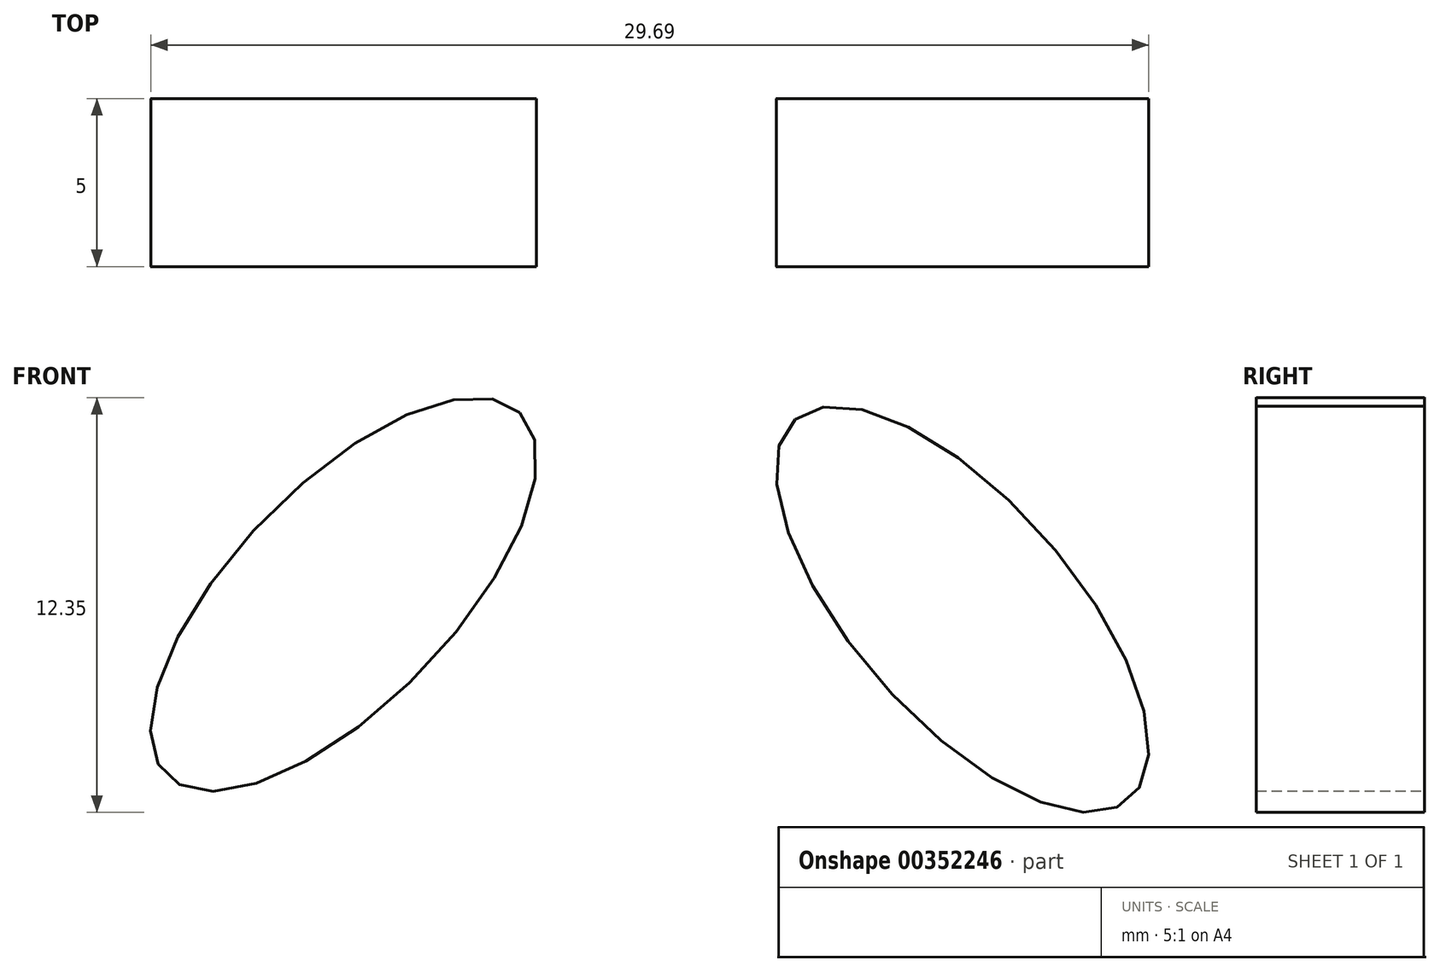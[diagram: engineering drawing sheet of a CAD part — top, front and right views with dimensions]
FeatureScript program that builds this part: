
annotation { "Feature Type Name" : "Feature", "Feature Type Description" : "" }
export const myFeature = defineFeature(function(context is Context, id is Id, definition is map)
    precondition{}
    {
        {
            var Q0;
            Q0=qCreatedBy(makeId("Front.planeOp"),FACE);
            var sketch = newSketch(context, id + "F0", { "sketchPlane" : qUnion([Q0])});
            skArc(sketch, "E0", {"start": v(-19.63, 15.48) * mm, "mid": v(-5.3, -24.43) * mm, "end": v(24.28, 5.97) * mm});
            skArc(sketch, "E1", {"start": v(-19.48, 0) * mm, "mid": v(1, -19.93) * mm, "end": v(21.47, 0) * mm});
            skFitSpline(sketch, "E2", {"points": [v(-19.48, 0) * mm, v(-9.63, -10.16) * mm, v(4.6, -12.46) * mm, v(15.7, -7.75) * mm, v(21.47, 0) * mm], "startDerivative": vector(32.51, -44.35) * mm, "endDerivative": vector(22.17, 38.02) * mm});
            skCircle(sketch, "E3", {"center": v(0, 0) * mm, "radius": 3.48 * mm});
            skFitSpline(sketch, "E4", {"points": [v(-19.63, 15.48) * mm, v(-28.7, 37.07) * mm, v(-14.36, 20.47) * mm, v(-13.3, 37.8) * mm, v(-6.26, 24.2) * mm, v(4.92, 39.9) * mm, v(10.04, 22.9) * mm, v(25.34, 32.04) * mm, v(20.75, 13.94) * mm, v(42.52, 12.46) * mm, v(24.28, 5.97) * mm], "startDerivative": vector(-151.91, 326.99) * mm, "endDerivative": vector(-305.53, -97.9) * mm});
            skArc(sketch, "E5.trimOffspring", {"start": v(-14.2, 20.57) * mm, "mid": v(-14.28, 20.52) * mm, "end": v(-14.36, 20.47) * mm});
            skArc(sketch, "E6.trimOffspring", {"start": v(-5.17, 24.46) * mm, "mid": v(-5.72, 24.34) * mm, "end": v(-6.26, 24.2) * mm});
            skArc(sketch, "E7.trimOffspring", {"start": v(10.04, 22.9) * mm, "mid": v(10, 22.9) * mm, "end": v(9.98, 22.92) * mm});
            skArc(sketch, "E8.trimOffspring", {"start": v(20.98, 13.6) * mm, "mid": v(20.86, 13.77) * mm, "end": v(20.75, 13.94) * mm});
            skSolve(sketch);
        }
        {
            var Q0;
            Q0=makeQuery(id+"F0.imprint","IMPRINT",FACE,{"disambiguationData":[TD([[makeQuery(id+"F0.imprint","IMPRINT",EDGE,{"derivedFrom":sQuery(id+"F0.wireOp",EDGE,"E0")}),1.0]])]});
            extrude(context, id + "F1", {"entities" : qUnion([Q0]), "flatOperationType" : FlatOperationType.REMOVE, "offsetDistance" : 25 * mm, "depth" : 5 * mm, "domain" : OperationDomain.MODEL});
        }
        {
            var Q0;
            Q0=makeQuery(id+"F1.opExtrude","CAP_FACE",FACE,{"disambiguationData":[OSD([sQuery(id+"F0.wireOp",EDGE,"E0"),sQuery(id+"F0.wireOp",EDGE,"E1"),sQuery(id+"F0.wireOp",EDGE,"E2"),sQuery(id+"F0.wireOp",EDGE,"E3"),sQuery(id+"F0.wireOp",EDGE,"E4"),sQuery(id+"F0.wireOp",EDGE,"E7.trimOffspring")])],"isStart":false});
            var sketch = newSketch(context, id + "F2", { "sketchPlane" : qUnion([Q0])});
            skEllipse(sketch, "E9", {"center": v(-8.95, 10.7) * mm, "majorRadius": 7.54 * mm, "minorRadius": 3.25 * mm, "majorAxis": v(0.7, 0.72)});
            skLineSegment(sketch, "E10", {"start": v(0, 0) * mm, "end": v(0.97, 40.13) * mm, "construction": true});
            skEllipse(sketch, "E11.MirrorC", {"center": v(9.46, 10.27) * mm, "majorRadius": 7.54 * mm, "minorRadius": 3.25 * mm, "majorAxis": v(-0.66, 0.75)});
            skSolve(sketch);
        }
        {
            var Q0;
            Q0=qSketchRegion(id+"F2",true);
            extrude(context, id + "F3", {"entities" : qUnion([Q0]), "operationType" : NewBodyOperationType.INTERSECT, "flatOperationType" : FlatOperationType.REMOVE, "thickness1" : 5 * mm, "thickness2" : 0 * mm, "thickness" : 5 * mm, "oppositeDirection" : true, "depth" : 10 * mm, "offsetDistance" : 25 * mm, "startOffsetBound" : StartOffsetType.BLIND, "startOffsetDistance" : 25 * mm, "domain" : OperationDomain.MODEL});
        }
    });
